# Revit family: LIXIL - 128-15 NV - COBRA STAR HEAVY PATTERN STOP TAP CONCEALED FEMALE 15MM _ FACE BASED
name_source: partatom
category: Plumbing Fixtures
units: mm (PartAtom-declared; Revit-internal decimal feet)

## family parameters
Cut with Voids When Loaded = No
Enable Cutting in Views = Yes
Host = Face
Maintain Annotation Orientation = No
OmniClass Number = 23.45.00.00
OmniClass Title = Sanitary, Laundry, and Cleaning Equipment
Part Type = Normal
Room Calculation Point = No
Round Connector Dimension = Use Diameter
Shared = Yes

## types (1)
- 128-15 NV
    Default Elevation = 1219 mm
    Description = Cobra Star Heavy Pattern Stop Tap Concealed Female 15mm to sanware schedule and spec. Available from Lixil.
    Hosted on lixil.co.za = https://www.lixil.co.za
    M _ BASIN = M _ LIXIL - VAAL - PORCELAIN - WHITE 01
    M _ WASTE = M _ LIXIL - STAINLESS STEEL 01
    Manufacturer = Cobra, supplied by Lixil
    Product Specification = Supplier: Lixil.
Product Description: Cobra Star Heavy Pattern Chrome plated stop tap including hot & cold indices. The original star-shaped design. Well-suited for use in low water pressure environments. 1/2" BSP female iron connection ends. Made with de-zincification resistant brass for increased durability. Cobra TeamAssist service team on call. Includes a 20 year LIXIL Africa warranty.
20 Year Warranty Cobra LowPressure Cobra TeamAssist DZR Brass 
Product Code: 1007890000.
SKU Code	: 128-15/NV.
Barcode: 6002194063827.
Brand: Cobra.
Range: Star Heavy Pattern.
Category: Taps.
Sub-Category: Baths. 
Material: DZR Brass.
Colour: Chrome.
Package Height: 85 mm
Package Width: 160 mm
Package Length: 160 mm
Package Volume: 2176 mm³
Package Weight: 630 g

Notes:
- Refer to manufacturer's and supplier's installation, maintenance and cleaning manual.
- Refer to manufacturer's and supplier's guarantees and warrantees document.
    Waste Connection Diameter = 45 mm  [stored 0.147638 ft]

note: [stored X ft] marks values corroborated as IEEE doubles in the binary element streams (Revit-internal decimal feet)

## geometry (parser evidence)
native form markers: Sweep x3
no freeform markers — native parametric forms only
